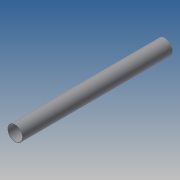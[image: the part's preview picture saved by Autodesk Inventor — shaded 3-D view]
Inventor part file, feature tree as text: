
AUTODESK INVENTOR PART (.ipt)
format: ipt  version: 2014 SP1 (Build 180222100, 222)  size: 73,728 bytes
history: native  units: in
note: dims shown in document units (in); Inventor stores cm internally (conversion verified against a paired STEP export)
features: extrude x1, sketch x1
ambient origin geometry x8: Origin, YZ Plane, XZ Plane, XY Plane, X Axis, Y Axis, Z Axis, Center Point
bodies: Solid1 (feature_tree)
feature tree (2):
  extrude  "Extrusion1"  Depth=59.0551in
  sketch  "Sketch1"  dims[d1=0.2in d2=6.0in d3=59.0551in d4=0.0in]
